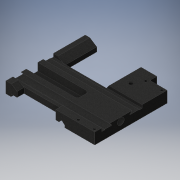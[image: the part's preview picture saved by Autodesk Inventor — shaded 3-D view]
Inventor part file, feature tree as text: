
AUTODESK INVENTOR PART (.ipt)
format: ipt  version: 2016 (Build 200138000, 138)  size: 307,712 bytes
history: native  units: in
note: dims shown in document units (in); Inventor stores cm internally (conversion verified against a paired STEP export)
features: extrude x15, sketch x12
ambient origin geometry x8: Origin, YZ Plane, XZ Plane, XY Plane, X Axis, Y Axis, Z Axis, Center Point
bodies: Solid1 (feature_tree)
feature tree (27):
  extrude  "Extrusion1"  Depth=13.5039in
  extrude  "Extrusion2"  Depth=1.9094in TaperAngle=0.0deg
  extrude  "Extrusion3"  Depth=1.378in
  extrude  "Extrusion4"  Depth=0.8933in
  extrude  "Extrusion8"  Depth=0.0787in
  extrude  "Extrusion19"  Depth=1.1811in
  extrude  "Extrusion20"  Depth=0.1181in
  extrude  "Extrusion21"  Depth=0.3937in
  extrude  "Extrusion22"  Depth=1.2992in
  extrude  "Extrusion23"  Depth=0.4567in
  extrude  "Extrusion24"  TaperAngle=0.0deg  [1 undecoded]
  extrude  "Extrusion25"  Depth=0.0787in TaperAngle=0.0deg
  extrude  "Extrusion26"  Depth=2.2441in
  extrude  "Extrusion27"  Depth=0.3937in TaperAngle=0.0deg
  extrude  "Extrusion28"  Depth=2.2441in
  sketch  "Sketch1"  dims[d0=15.1181in d1=13.5039in]
  sketch  "Sketch12"  dims[d2=1.9094in d3=0.0in d12=1.9094in d13=0.0in]
  sketch  "Sketch28"  dims[d23=1.378in d27=3.7795in]
  sketch  "Sketch29"  dims[d29=1.7323in d32=0.8933in]
  sketch  "Sketch30"  dims[d35=1.9094in d36=0.0in d37=0.0787in]
  sketch  "Sketch32"  dims[d38=0.5118in d43=1.1811in]
  sketch  "Sketch36"  dims[d44=1.9094in d45=0.0in d46=0.1181in]
  sketch  "Sketch37"  dims[d52=0.3436in d72=0.3937in]
  sketch  "Sketch38"  dims[d73=1.2992in d74=0.0in d146=0.4567in]
  sketch  "Sketch40"  dims[d149=0.4567in d152=0.4567in]
  sketch  "Sketch41"  dims[d155=0.4567in d156=0.0in d157=0.0in]
  sketch  "Sketch42"  dims[d159=0.0787in d160=0.0in d161=0.0787in d162=0.0in d168=0.6299in d169=0.3937in d170=0.0in d209=0.6299in d210=45.0deg d211=0.1811in d214=0.5197in d215=45.0deg d216=0.4724in d224=0.8661in d225=0.3937in d227=0.3937in d228=0.0in d229=0.5512in d232=0.748in d233=5.5118in d234=0.0in d235=5.5118in d236=0.0in d240=0.5197in d242=0.1811in d243=0.6299in d245=5.5118in d246=0.0in d247=0.6693in d248=0.3937in d249=0.0in d250=1.1417in d251=2.2441in d252=0.0in]
note: 1 required parameter value undecoded (feature->parameter linkage not recoverable at this tier; creation-order binding heuristic only, values carry confidence <= 0.55)
